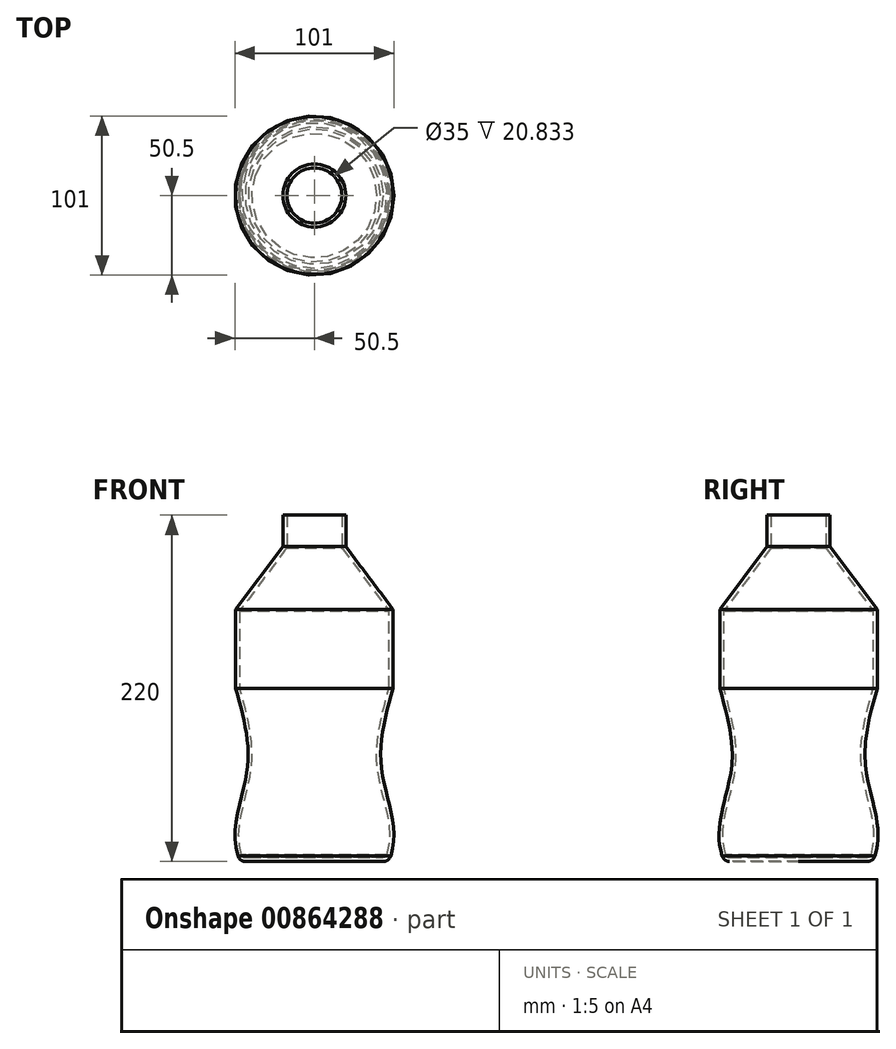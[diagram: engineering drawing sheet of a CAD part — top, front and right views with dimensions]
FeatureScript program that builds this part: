
annotation { "Feature Type Name" : "Feature", "Feature Type Description" : "" }
export const myFeature = defineFeature(function(context is Context, id is Id, definition is map)
    precondition{}
    {
        {
            var Q0;
            Q0=qCreatedBy(makeId("Top.planeOp"),FACE);
            var sketch = newSketch(context, id + "F0", { "sketchPlane" : qUnion([Q0])});
            skCircle(sketch, "E0", {"center": v(0, 0) * mm, "radius": 50 * mm});
            skSolve(sketch);
        }
        {
            var Q0;
            Q0=qCreatedBy(makeId("Top.planeOp"),FACE);
            cPlane(context, id + "F1", {"entities" : qUnion([Q0]), "cplaneType" : CPlaneType.OFFSET, "offset" : 50 * mm, "width" : 150 * mm, "height" : 150 * mm});
        }
        {
            var Q0;
            Q0=qCreatedBy(id+"F1.planeOp",FACE);
            cPlane(context, id + "F2", {"entities" : qUnion([Q0]), "cplaneType" : CPlaneType.OFFSET, "offset" : 50 * mm, "width" : 150 * mm, "height" : 150 * mm});
        }
        {
            var Q0;
            Q0=qCreatedBy(id+"F1.planeOp",FACE);
            var sketch = newSketch(context, id + "F3", { "sketchPlane" : qUnion([Q0])});
            skCircle(sketch, "E1", {"center": v(0, 0) * mm, "radius": 42.5 * mm});
            skSolve(sketch);
        }
        {
            var Q0;
            Q0=qCreatedBy(id+"F2.planeOp",FACE);
            var sketch = newSketch(context, id + "F4", { "sketchPlane" : qUnion([Q0])});
            skCircle(sketch, "E2", {"center": v(0, 0) * mm, "radius": 50 * mm});
            skSolve(sketch);
        }
        {
            var Q0;
            Q0=qCreatedBy(makeId("Top.planeOp"),FACE);
            cPlane(context, id + "F5", {"entities" : qUnion([Q0]), "cplaneType" : CPlaneType.OFFSET, "offset" : 10 * mm, "oppositeDirection" : true, "width" : 150 * mm, "height" : 150 * mm});
        }
        {
            var Q0;
            Q0=qCreatedBy(id+"F5.planeOp",FACE);
            var sketch = newSketch(context, id + "F6", { "sketchPlane" : qUnion([Q0])});
            skCircle(sketch, "E3", {"center": v(0, 0) * mm, "radius": 47.5 * mm});
            skSolve(sketch);
        }
        {
            var Q0;
            Q0=qCreatedBy(id+"F2.planeOp",FACE);
            cPlane(context, id + "F7", {"entities" : qUnion([Q0]), "cplaneType" : CPlaneType.OFFSET, "offset" : 50 * mm, "width" : 150 * mm, "height" : 150 * mm});
        }
        {
            var Q0;
            Q0=qCreatedBy(id+"F7.planeOp",FACE);
            var sketch = newSketch(context, id + "F8", { "sketchPlane" : qUnion([Q0])});
            skCircle(sketch, "E4", {"center": v(0, 0) * mm, "radius": 50 * mm});
            skSolve(sketch);
        }
        {
            var Q0;
            Q0=qCreatedBy(id+"F7.planeOp",FACE);
            cPlane(context, id + "F9", {"entities" : qUnion([Q0]), "cplaneType" : CPlaneType.OFFSET, "offset" : 40 * mm, "width" : 150 * mm, "height" : 150 * mm});
        }
        {
            var Q0;
            Q0=qCreatedBy(id+"F9.planeOp",FACE);
            var sketch = newSketch(context, id + "F10", { "sketchPlane" : qUnion([Q0])});
            skCircle(sketch, "E5", {"center": v(0, 0) * mm, "radius": 20 * mm});
            skSolve(sketch);
        }
        {
            var Q0;
            Q0=makeQuery(id+"F6.imprint","IMPRINT",FACE,{"disambiguationData":[TD([[makeQuery(id+"F6.imprint","IMPRINT",EDGE,{"derivedFrom":sQuery(id+"F6.wireOp",EDGE,"E3")}),1.0]])]});
            var Q1;
            Q1=makeQuery(id+"F0.imprint","IMPRINT",FACE,{"disambiguationData":[TD([[makeQuery(id+"F0.imprint","IMPRINT",EDGE,{"derivedFrom":sQuery(id+"F0.wireOp",EDGE,"E0")}),1.0]])]});
            var Q2;
            Q2=makeQuery(id+"F3.imprint","IMPRINT",FACE,{"disambiguationData":[TD([[makeQuery(id+"F3.imprint","IMPRINT",EDGE,{"derivedFrom":sQuery(id+"F3.wireOp",EDGE,"E1")}),1.0]])]});
            var Q3;
            Q3=makeQuery(id+"F4.imprint","IMPRINT",FACE,{"disambiguationData":[TD([[makeQuery(id+"F4.imprint","IMPRINT",EDGE,{"derivedFrom":sQuery(id+"F4.wireOp",EDGE,"E2")}),1.0]])]});
            loft(context, id + "F11", {"sheetProfilesArray" : [{ "sheetProfileEntities" : qUnion([Q0]) }, { "sheetProfileEntities" : qUnion([Q1]) }, { "sheetProfileEntities" : qUnion([Q2]) }, { "sheetProfileEntities" : qUnion([Q3]) }]});
        }
        {
            var Q0;
            Q0=makeQuery(id+"F11.opLoft","CAP_FACE",FACE,{"disambiguationData":[OSD([makeQuery(id+"F4.imprint","IMPRINT",FACE,{"disambiguationData":[TD([[makeQuery(id+"F4.imprint","IMPRINT",EDGE,{"derivedFrom":sQuery(id+"F4.wireOp",EDGE,"E2")}),1.0]])]})])],"isStart":true});
            var Q1;
            Q1=qCreatedBy(id+"F7.planeOp",FACE);
            extrude(context, id + "F12", {"entities" : qUnion([Q0]), "operationType" : NewBodyOperationType.ADD, "endBound" : BoundingType.UP_TO_SURFACE, "depth" : 25 * mm, "endBoundEntityFace" : qUnion([Q1]), "offsetDistance" : 25 * mm});
        }
        {
            var Q1;
            Q1=makeQuery(id+"F8.imprint","IMPRINT",FACE,{"disambiguationData":[TD([[makeQuery(id+"F8.imprint","IMPRINT",EDGE,{"derivedFrom":sQuery(id+"F8.wireOp",EDGE,"E4")}),1.0]])]});
            var Q2;
            Q2=makeQuery(id+"F10.imprint","IMPRINT",FACE,{"disambiguationData":[TD([[makeQuery(id+"F10.imprint","IMPRINT",EDGE,{"derivedFrom":sQuery(id+"F10.wireOp",EDGE,"E5")}),1.0]])]});
            loft(context, id + "F13", {"operationType" : NewBodyOperationType.ADD, "sheetProfilesArray" : [{ "sheetProfileEntities" : qUnion([Q1]) }, { "sheetProfileEntities" : qUnion([Q2]) }]});
        }
        {
            var Q0;
            Q0=makeQuery(id+"F13.opLoft","CAP_FACE",FACE,{"disambiguationData":[OSD([makeQuery(id+"F10.imprint","IMPRINT",FACE,{"disambiguationData":[TD([[makeQuery(id+"F10.imprint","IMPRINT",EDGE,{"derivedFrom":sQuery(id+"F10.wireOp",EDGE,"E5")}),1.0]])]})])],"isStart":true});
            extrude(context, id + "F14", {"entities" : qUnion([Q0]), "operationType" : NewBodyOperationType.ADD, "depth" : 20 * mm, "offsetDistance" : 25 * mm});
        }
        {
            var Q0;
            Q0=makeQuery(id+"F11.opLoft","CAP_FACE",FACE,{"disambiguationData":[OSD([makeQuery(id+"F6.imprint","IMPRINT",FACE,{"disambiguationData":[TD([[makeQuery(id+"F6.imprint","IMPRINT",EDGE,{"derivedFrom":sQuery(id+"F6.wireOp",EDGE,"E3")}),1.0]])]})])],"isStart":true});
            fillet(context, id + "F15", {"entities" : qUnion([Q0]), "radius" : 5 * mm, "tangentPropagation" : true, "allowEdgeOverflow" : false});
        }
        {
            var Q0;
            Q0=makeQuery(id+"F14.opExtrude","CAP_FACE",FACE,{"disambiguationData":[OSD([makeQuery(id+"F10.imprint","IMPRINT",FACE,{"disambiguationData":[TD([[makeQuery(id+"F10.imprint","IMPRINT",EDGE,{"derivedFrom":sQuery(id+"F10.wireOp",EDGE,"E5")}),1.0]])]})])],"isStart":false});
            shell(context, id + "F16", {"entities" : qUnion([Q0]), "thickness" : 2.5 * mm});
        }
    });
